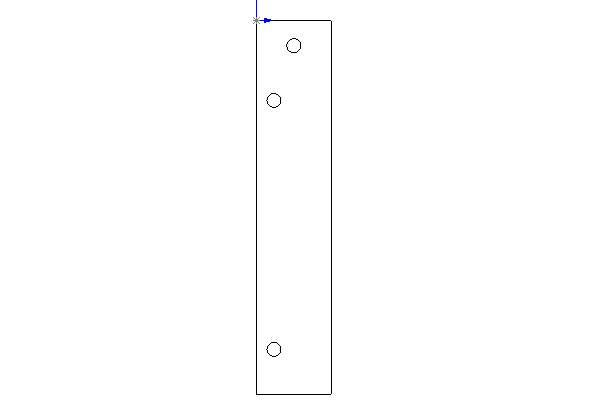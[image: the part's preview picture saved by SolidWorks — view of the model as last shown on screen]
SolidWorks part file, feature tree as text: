
SOLIDWORKS PART (.sldprt)
format: sldprt  version: not decoded by parser v0  size: 147,456 bytes
history: native  units: mm
features: sketch x3, cut_extrude x2, material x1, extrude x1 (+13 scaffold rows collapsed)
feature tree (20):
  scaffold x13  (default folders/planes/origin — collapsed)
  material  "Material <not specified>"
  sketch  "Sketch1"  dims[D1=19.05mm D2=95.25mm]
  extrude  "Extrude1"  Depth=1.6002mm
  sketch  "Sketch2"  dims[D1=3.6068mm D2=3.5052mm D3=9.525mm D4=6.35mm D5=9.525mm D6=6.35mm]
  cut_extrude  "Cut-Extrude1"  Depth=1.6002mm
  sketch  "Sketch3"  dims[D1=3.556mm D2=3.556mm D3=11.43mm D4=4.445mm D5=63.5mm]
  cut_extrude  "Cut-Extrude2"  Depth=2.54mm
decode coverage: 6 of 6 modeling features carry decoded parameters
note: suppression state not decoded; provenance and decode notes live in map.json
